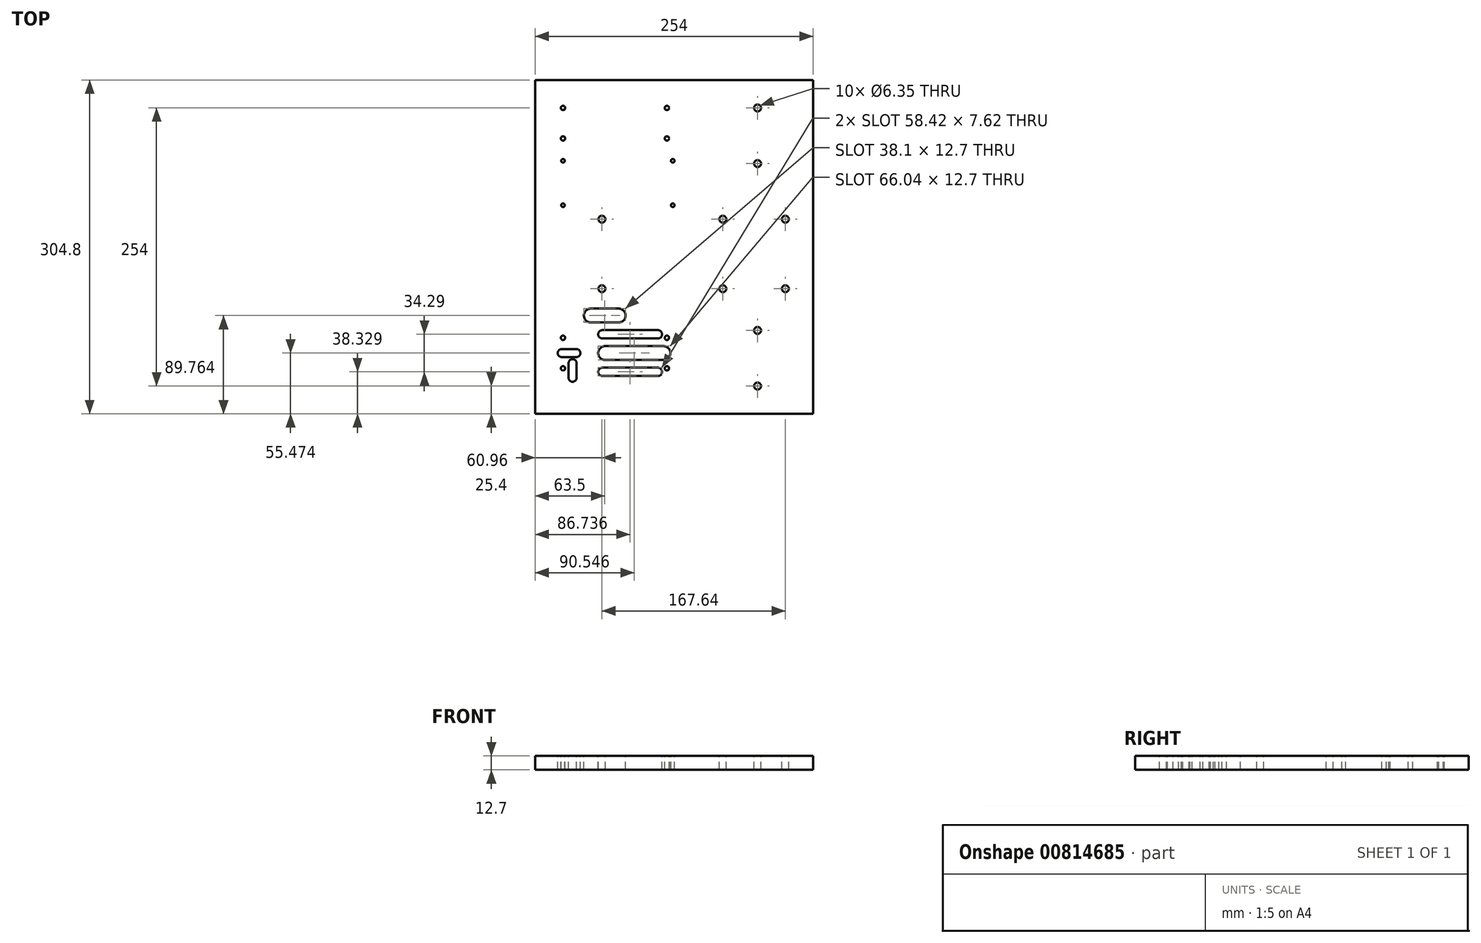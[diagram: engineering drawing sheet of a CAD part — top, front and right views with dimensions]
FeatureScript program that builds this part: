
annotation { "Feature Type Name" : "Feature", "Feature Type Description" : "" }
export const myFeature = defineFeature(function(context is Context, id is Id, definition is map)
    precondition{}
    {
        {
            var Q0;
            Q0=qCreatedBy(makeId("Top.planeOp"),FACE);
            var sketch = newSketch(context, id + "F0", { "sketchPlane" : qUnion([Q0])});
            skLineSegment(sketch, "E0.bottom", {"start": v(127, 152.4) * mm, "end": v(-127, 152.4) * mm});
            skLineSegment(sketch, "E0.top", {"start": v(127, -152.4) * mm, "end": v(-127, -152.4) * mm});
            skLineSegment(sketch, "E0.left", {"start": v(127, 152.4) * mm, "end": v(127, -152.4) * mm});
            skLineSegment(sketch, "E0.right", {"start": v(-127, 152.4) * mm, "end": v(-127, -152.4) * mm});
            skPoint(sketch, "E0.middle", {"position": v(0, 0) * mm});
            skSolve(sketch);
        }
        {
            var Q0;
            Q0=makeQuery(id+"F0.imprint","IMPRINT",FACE,{"disambiguationData":[TD([[makeQuery(id+"F0.imprint","IMPRINT",EDGE,{"derivedFrom":sQuery(id+"F0.wireOp",EDGE,"E0.bottom")}),1.0]])]});
            extrude(context, id + "F1", {"entities" : qUnion([Q0]), "depth" : 12.7 * mm, "offsetDistance" : 25.4 * mm});
        }
        {
            var Q0;
            Q0=makeQuery(id+"F1.opExtrude","CAP_FACE",FACE,{"disambiguationData":[OSD([sQuery(id+"F0.wireOp",EDGE,"E0.bottom"),sQuery(id+"F0.wireOp",EDGE,"E0.top"),sQuery(id+"F0.wireOp",EDGE,"E0.left"),sQuery(id+"F0.wireOp",EDGE,"E0.right")])],"isStart":false});
            var sketch = newSketch(context, id + "F2", { "sketchPlane" : qUnion([Q0])});
            skCircle(sketch, "E1", {"center": v(-101.6, 127) * mm, "radius": 1.98 * mm});
            skCircle(sketch, "E2", {"center": v(-101.6, 99.11) * mm, "radius": 1.98 * mm});
            skCircle(sketch, "E3", {"center": v(-6.6, 127) * mm, "radius": 1.98 * mm});
            skCircle(sketch, "E4", {"center": v(-6.6, 99.11) * mm, "radius": 1.98 * mm});
            skCircle(sketch, "E5", {"center": v(-101.6, -82.97) * mm, "radius": 1.98 * mm});
            skCircle(sketch, "E6", {"center": v(-6.6, -82.97) * mm, "radius": 1.98 * mm});
            skCircle(sketch, "E7", {"center": v(-6.6, -110.86) * mm, "radius": 1.98 * mm});
            skCircle(sketch, "E8", {"center": v(-101.6, -110.86) * mm, "radius": 1.98 * mm});
            skCircle(sketch, "E9", {"center": v(-101.6, 78.74) * mm, "radius": 1.65 * mm});
            skCircle(sketch, "E10", {"center": v(-101.6, 38.12) * mm, "radius": 1.65 * mm});
            skCircle(sketch, "E11", {"center": v(-66.04, 25.4) * mm, "radius": 3.18 * mm});
            skCircle(sketch, "E12", {"center": v(-66.04, -38.1) * mm, "radius": 3.18 * mm});
            skCircle(sketch, "E13", {"center": v(76.2, -76.2) * mm, "radius": 3.18 * mm});
            skCircle(sketch, "E14", {"center": v(76.2, -127) * mm, "radius": 3.18 * mm});
            skCircle(sketch, "E15", {"center": v(76.2, 127) * mm, "radius": 3.18 * mm});
            skCircle(sketch, "E16", {"center": v(76.2, 76.2) * mm, "radius": 3.18 * mm});
            skCircle(sketch, "E17", {"center": v(44.45, 25.4) * mm, "radius": 3.18 * mm});
            skCircle(sketch, "E18", {"center": v(101.6, 25.4) * mm, "radius": 3.18 * mm});
            skCircle(sketch, "E19", {"center": v(44.45, -38.1) * mm, "radius": 3.18 * mm});
            skCircle(sketch, "E20", {"center": v(101.6, -38.1) * mm, "radius": 3.18 * mm});
            skLineSegment(sketch, "E21.bottom", {"start": v(-63.12, -90.58) * mm, "end": v(-9.78, -90.58) * mm});
            skLineSegment(sketch, "E21.top", {"start": v(-63.12, -103.28) * mm, "end": v(-9.78, -103.28) * mm});
            skLineSegment(sketch, "E21.left", {"start": v(-63.12, -90.58) * mm, "end": v(-63.12, -103.28) * mm});
            skLineSegment(sketch, "E21.right", {"start": v(-9.78, -90.58) * mm, "end": v(-9.78, -103.28) * mm});
            skLineSegment(sketch, "E22.bottom", {"start": v(-65.66, -110.26) * mm, "end": v(-14.86, -110.26) * mm});
            skLineSegment(sketch, "E22.top", {"start": v(-65.66, -117.88) * mm, "end": v(-14.86, -117.88) * mm});
            skLineSegment(sketch, "E22.left", {"start": v(-65.66, -110.26) * mm, "end": v(-65.66, -117.88) * mm});
            skLineSegment(sketch, "E22.right", {"start": v(-14.86, -110.26) * mm, "end": v(-14.86, -117.88) * mm});
            skLineSegment(sketch, "E23.bottom", {"start": v(-76.2, -56.29) * mm, "end": v(-50.8, -56.29) * mm});
            skLineSegment(sketch, "E23.top", {"start": v(-76.2, -68.99) * mm, "end": v(-50.8, -68.99) * mm});
            skLineSegment(sketch, "E23.left", {"start": v(-76.2, -56.29) * mm, "end": v(-76.2, -68.99) * mm});
            skLineSegment(sketch, "E23.right", {"start": v(-50.8, -56.29) * mm, "end": v(-50.8, -68.99) * mm});
            skLineSegment(sketch, "E24.bottom", {"start": v(-65.66, -75.97) * mm, "end": v(-14.86, -75.97) * mm});
            skLineSegment(sketch, "E24.top", {"start": v(-65.66, -83.6) * mm, "end": v(-14.86, -83.6) * mm});
            skLineSegment(sketch, "E24.left", {"start": v(-65.66, -75.97) * mm, "end": v(-65.66, -83.6) * mm});
            skLineSegment(sketch, "E24.right", {"start": v(-14.86, -75.97) * mm, "end": v(-14.86, -83.6) * mm});
            skLineSegment(sketch, "E25", {"start": v(-63.12, -103.28) * mm, "end": v(-63.12, -96.93) * mm});
            skCircle(sketch, "E26", {"center": v(-1.29, 78.74) * mm, "radius": 1.65 * mm});
            skCircle(sketch, "E27", {"center": v(-1.29, 38.12) * mm, "radius": 1.65 * mm});
            skArc(sketch, "E28", {"start": v(-63.12, -90.58) * mm, "mid": v(-69.47, -96.93) * mm, "end": v(-63.12, -103.28) * mm});
            skArc(sketch, "E29", {"start": v(-9.78, -103.28) * mm, "mid": v(-3.43, -96.93) * mm, "end": v(-9.78, -90.58) * mm});
            skArc(sketch, "E30", {"start": v(-65.66, -75.97) * mm, "mid": v(-69.47, -79.78) * mm, "end": v(-65.66, -83.6) * mm});
            skArc(sketch, "E31", {"start": v(-14.86, -83.6) * mm, "mid": v(-11.05, -79.78) * mm, "end": v(-14.86, -75.97) * mm});
            skArc(sketch, "E32", {"start": v(-14.86, -117.88) * mm, "mid": v(-11.05, -114.07) * mm, "end": v(-14.86, -110.26) * mm});
            skArc(sketch, "E33", {"start": v(-65.66, -110.26) * mm, "mid": v(-69.47, -114.07) * mm, "end": v(-65.66, -117.88) * mm});
            skArc(sketch, "E34", {"start": v(-50.8, -68.99) * mm, "mid": v(-44.45, -62.64) * mm, "end": v(-50.8, -56.29) * mm});
            skArc(sketch, "E35", {"start": v(-76.2, -56.29) * mm, "mid": v(-82.55, -62.64) * mm, "end": v(-76.2, -68.99) * mm});
            skLineSegment(sketch, "E36.bottom", {"start": v(-96.52, -106.1) * mm, "end": v(-89.16, -106.1) * mm});
            skLineSegment(sketch, "E36.top", {"start": v(-96.52, -119.44) * mm, "end": v(-89.16, -119.44) * mm});
            skLineSegment(sketch, "E36.left", {"start": v(-96.52, -106.1) * mm, "end": v(-96.52, -119.44) * mm});
            skLineSegment(sketch, "E36.right", {"start": v(-89.16, -106.1) * mm, "end": v(-89.16, -119.44) * mm});
            skLineSegment(sketch, "E37.bottom", {"start": v(-89.4, -93.2) * mm, "end": v(-102.74, -93.2) * mm});
            skLineSegment(sketch, "E37.top", {"start": v(-89.4, -100.57) * mm, "end": v(-102.74, -100.57) * mm});
            skLineSegment(sketch, "E37.left", {"start": v(-89.4, -93.2) * mm, "end": v(-89.4, -100.57) * mm});
            skLineSegment(sketch, "E37.right", {"start": v(-102.74, -93.2) * mm, "end": v(-102.74, -100.57) * mm});
            skArc(sketch, "E38", {"start": v(-89.16, -106.1) * mm, "mid": v(-92.84, -102.43) * mm, "end": v(-96.52, -106.1) * mm});
            skArc(sketch, "E39", {"start": v(-96.52, -119.44) * mm, "mid": v(-92.84, -123.12) * mm, "end": v(-89.16, -119.44) * mm});
            skArc(sketch, "E40", {"start": v(-89.4, -100.57) * mm, "mid": v(-85.72, -96.88) * mm, "end": v(-89.4, -93.2) * mm});
            skArc(sketch, "E41", {"start": v(-102.74, -93.2) * mm, "mid": v(-106.43, -96.88) * mm, "end": v(-102.74, -100.57) * mm});
            skSolve(sketch);
        }
        {
            var Q0;
            Q0=qSketchRegion(id+"F2",true);
            extrude(context, id + "F3", {"entities" : qUnion([Q0]), "operationType" : NewBodyOperationType.REMOVE, "oppositeDirection" : true, "depth" : 25.4 * mm, "offsetDistance" : 25.4 * mm});
        }
    });
